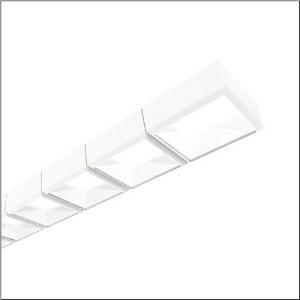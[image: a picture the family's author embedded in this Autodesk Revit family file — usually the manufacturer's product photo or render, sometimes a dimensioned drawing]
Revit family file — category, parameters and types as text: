
# Revit family: scriptus_r__11_5mz223d04wa_758a
name_source: partatom
category: Lighting Fixtures
units: mm (PartAtom-declared; Revit-internal decimal feet)

## family parameters
Cut with Voids When Loaded = No
Host = Face
Light Source = No
Part Type = Normal
Room Calculation Point = No
Round Connector Dimension = Use Diameter
Shared = No

## types (1)
- --- (1 x LED 4000K / CRI = 80 (unbekannt), 7230 lm, 4000K)
    Apparent Load = 51 VA
    CIE Flux Codes = 82 95 99 100 100
    Color Rendering = 80
    Color Temperature = 4000K
    Default Elevation = 1800 mm
    Description = Scriptus® 11, office luminaire, primary optical cover: lenses, CAT 2 (L<= 3000cd/m²), light emission: direct distribution, primary light characteristic: symmetric, installation type: surface-mounted, LED, rated luminous flux: 7.230lm, luminous efficacy: 143lm/W, light colour: 840, colour temperature: 4000K, control gear: DALI, with terminal, 5-pole, mains connection: 230V, AC, 50Hz, rated input power: 51W, housing, luminaire housing, of aluminium, traffic white (RAL 9016), length: 2.426mm, width: 114mm, height: 57mm, protection rating (complete): IP20, insulation class (complete): insulation class I (protective earthing), certification: CE, ENEC, VDE, protection symbol: F, permissible operating ambient temperature: 0..+35°C, standard: EN 50419, packaging unit: 1 piece
    Height = 57 mm
    Lamp = 1 x LED 4000K / CRI >= 80 (unbekannt)
    Lamp Light Flux = 7230 lm
    Lamp count = 1
    Length = 2426 mm
    Luminous efficacy = 143 lm/W
    Manufacturer = Siteco
    ModVariant = No
    Model = 5MZ223D04WA
    Mounting Place = Ceiling
    Mounting Type = Surface mounted
    Number of Poles = 1
    OnlyDefault = Yes
    Power Factor = 1
    Product Name = Scriptus® 11
    Product group = office luminaire | ceiling mounted
    ProductGroupID = 303
    Protection Class = Protection class I
    Protection Degree = IP 20
    RLX_Detail_Level = 1
    RLX_Emergency_Light_Flux = 0 lm
    RLX_Emergency_Type = 0
    RLX_Emergency_Type_DB = No
    RlxData = <blob elided: 31365 chars, md5=ee3d87ba>
    Socket = socket
    Standby Power = 0 W
    System Light Flux = 7230 lm
    System Power = 51 W
    Type Comments = factory setting: luminous flux: 100 % | dim-lin: 254 | 525 mA
    Type Image = l_1004833.jpg
    URL = http://relux.com
    VarID = @adj_220149
    Voltage = 0 V
    Weight = 0.00 kg
    Width = 114 mm

## geometry (parser evidence)
native form markers: Blend x4, Sweep x7
no freeform markers — native parametric forms only
